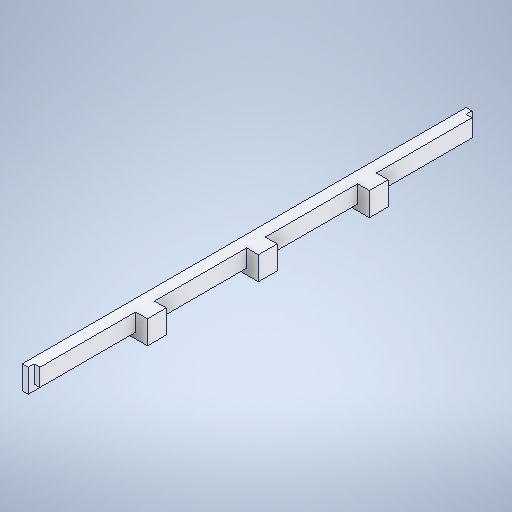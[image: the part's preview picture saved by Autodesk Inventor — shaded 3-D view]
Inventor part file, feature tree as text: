
AUTODESK INVENTOR PART (.ipt)
format: ipt  version: 2025 (Build 290162000, 162)  size: 383,488 bytes
history: native  units: in
note: dims shown in document units (in); Inventor stores cm internally (conversion verified against a paired STEP export)
features: extrude x8, sketch x8, projected_geometry x8
ambient origin geometry x8: Origin, YZ Plane, XZ Plane, XY Plane, X Axis, Y Axis, Z Axis, Center Point
bodies: Solid1 (feature_tree)
feature tree (24):
  extrude  "Extrusion1"  Depth=5.9213in
  extrude  "Extrusion2"  Depth=0.0787in
  extrude  "Extrusion3"  Depth=0.0787in
  extrude  "Extrusion4"  Depth=0.25in
  extrude  "Extrusion5"  Depth=0.25in
  extrude  "Extrusion6"  Depth=0.0787in TaperAngle=0.0deg
  extrude  "Extrusion7"  Depth=0.0787in TaperAngle=0.0deg
  extrude  "Extrusion8"  Depth=0.1772in
  sketch  "Sketch1"  dims[d0=2.75in d1=5.9213in]
  sketch  "Sketch2"  dims[d2=0.0787in d3=0.0in d4=0.0787in]
  projected_geometry  "Projected Loop1"
  sketch  "Sketch3"  dims[d5=0.0787in d6=0.0787in]
  projected_geometry  "Projected Loop2"
  sketch  "Sketch4"  dims[d7=0.0787in d8=0.0in d9=0.25in]
  projected_geometry  "Projected Loop3"
  sketch  "Sketch5"  dims[d10=0.25in d11=0.25in]
  projected_geometry  "Projected Loop4"
  sketch  "Sketch7"  dims[d12=0.1575in d13=0.0in d14=0.0787in d15=0.0in]
  projected_geometry  "Projected Loop5"
  projected_geometry  "Projected Loop6"
  projected_geometry  "Projected Loop7"
  sketch  "Sketch8"  dims[d16=0.0787in d17=0.0in d18=0.0787in d19=0.0in]
  projected_geometry  "Projected Loop8"
  sketch  "Sketch9"  dims[d20=0.1772in d21=0.1772in d22=0.1969in d23=0.0in d24=2.4375in d25=0.0in]
